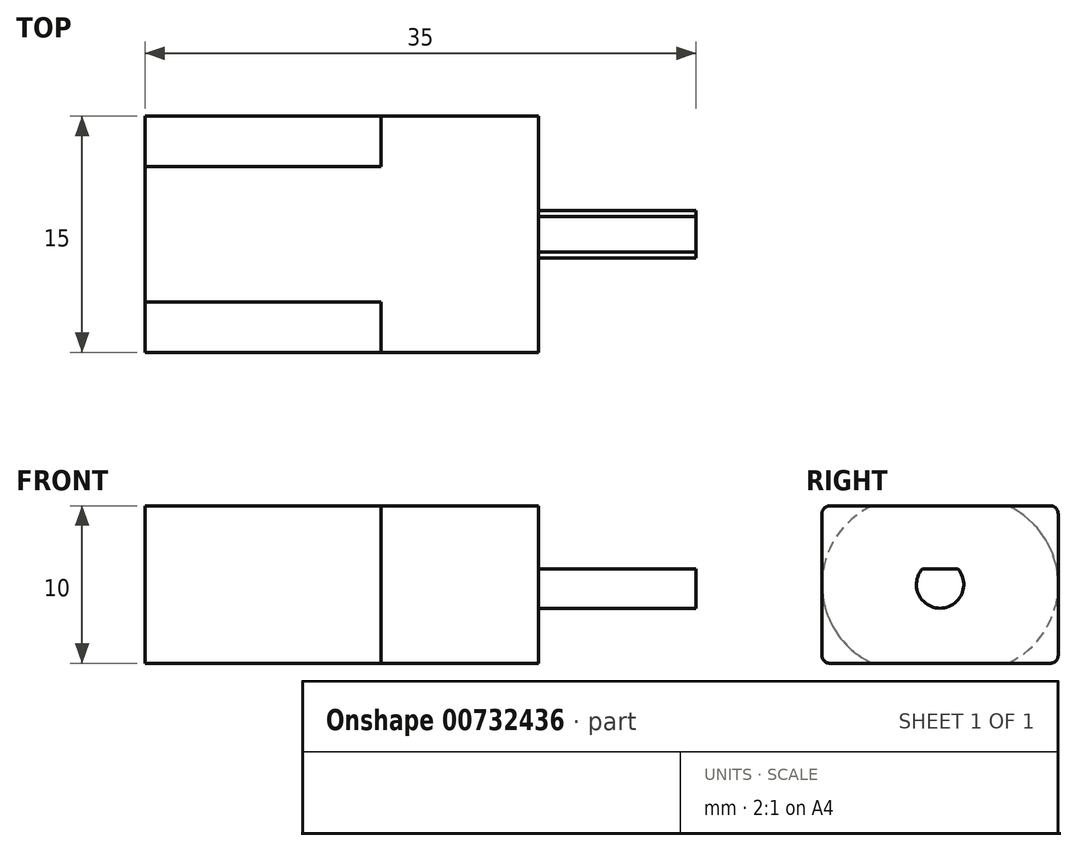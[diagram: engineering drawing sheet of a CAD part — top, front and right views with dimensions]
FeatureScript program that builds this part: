
annotation { "Feature Type Name" : "Feature", "Feature Type Description" : "" }
export const myFeature = defineFeature(function(context is Context, id is Id, definition is map)
    precondition{}
    {
        {
            var Q0;
            Q0=qCreatedBy(makeId("Right.planeOp"),FACE);
            var sketch = newSketch(context, id + "F0", { "sketchPlane" : qUnion([Q0])});
            skLineSegment(sketch, "E0.bottom", {"start": v(-4.3, 5) * mm, "end": v(4.3, 5) * mm});
            skLineSegment(sketch, "E0.top", {"start": v(-4.3, -5) * mm, "end": v(4.3, -5) * mm});
            skLineSegment(sketch, "E1", {"start": v(0, 5) * mm, "end": v(0, 0) * mm, "construction": true});
            skLineSegment(sketch, "E2", {"start": v(0, 0) * mm, "end": v(0, -5) * mm, "construction": true});
            skLineSegment(sketch, "E3", {"start": v(-7.5, 0) * mm, "end": v(0, 0) * mm, "construction": true});
            skLineSegment(sketch, "E4", {"start": v(7.5, 0) * mm, "end": v(0, 0) * mm, "construction": true});
            skArc(sketch, "E5", {"start": v(4.3, -5) * mm, "mid": v(7.5, 0) * mm, "end": v(4.3, 5) * mm});
            skArc(sketch, "E6.MirrorCS", {"start": v(-4.3, -5) * mm, "mid": v(-7.5, 0) * mm, "end": v(-4.3, 5) * mm});
            skSolve(sketch);
        }
        {
            var Q0;
            Q0=makeQuery(id+"F0.imprint","IMPRINT",FACE,{"disambiguationData":[TD([[makeQuery(id+"F0.imprint","IMPRINT",EDGE,{"derivedFrom":sQuery(id+"F0.wireOp",EDGE,"E0.bottom")}),-1.0]])]});
            extrude(context, id + "F1", {"entities" : qUnion([Q0]), "depth" : 15 * mm, "offsetDistance" : 25 * mm});
        }
        {
            var Q0;
            Q0=makeQuery(id+"F1.opExtrude","CAP_FACE",FACE,{"disambiguationData":[OSD([sQuery(id+"F0.wireOp",EDGE,"E0.bottom"),sQuery(id+"F0.wireOp",EDGE,"E0.top"),sQuery(id+"F0.wireOp",EDGE,"E5"),sQuery(id+"F0.wireOp",EDGE,"E6.MirrorCS")])],"isStart":false});
            var sketch = newSketch(context, id + "F2", { "sketchPlane" : qUnion([Q0])});
            skPoint(sketch, "E7.firstSnap0", {"position": v(-7.5, 0) * mm});
            skPoint(sketch, "E7.oppositeSnap0", {"position": v(7.5, 0) * mm});
            skLineSegment(sketch, "E7.bottom", {"start": v(-7.5, 5) * mm, "end": v(7.5, 5) * mm});
            skLineSegment(sketch, "E7.top", {"start": v(-7.5, -5) * mm, "end": v(7.5, -5) * mm});
            skLineSegment(sketch, "E7.left", {"start": v(-7.5, 5) * mm, "end": v(-7.5, -5) * mm});
            skLineSegment(sketch, "E7.right", {"start": v(7.5, 5) * mm, "end": v(7.5, -5) * mm});
            skSolve(sketch);
        }
        {
            var Q0;
            {var subQ0=sQuery(id+"F2.wireOp",EDGE,"E7.bottom");var subQ1=makeQuery(id+"F1.opExtrude","CAP_EDGE",EDGE,{"disambiguationData":[OSD([sQuery(id+"F0.wireOp",EDGE,"E6.MirrorCS")])],"isStart":false});var subQ2=makeQuery(id+"F2.imprint","INTERSECT",VERTEX,{"derivedFrom":[subQ1,subQ0]});Q0=makeQuery(id+"F2.imprint","IMPRINT",FACE,{"disambiguationData":[TD([[makeQuery(id+"F2.imprint","IMPRINT",EDGE,{"disambiguationData":[TD([[subQ2,1.0]])],"derivedFrom":subQ0}),-1.0]])]});}
            var Q1;
            {var subQ0=sQuery(id+"F2.wireOp",EDGE,"E7.bottom");var subQ1=makeQuery(id+"F1.opExtrude","CAP_EDGE",EDGE,{"disambiguationData":[OSD([sQuery(id+"F0.wireOp",EDGE,"E5")])],"isStart":false});var subQ2=makeQuery(id+"F2.imprint","INTERSECT",VERTEX,{"derivedFrom":[subQ1,subQ0]});Q1=makeQuery(id+"F2.imprint","IMPRINT",FACE,{"disambiguationData":[TD([[makeQuery(id+"F2.imprint","IMPRINT",EDGE,{"disambiguationData":[TD([[subQ2,-1.0]])],"derivedFrom":subQ0}),-1.0]])]});}
            var Q2;
            {var subQ0=sQuery(id+"F2.wireOp",EDGE,"E7.bottom");var subQ5=makeQuery(id+"F1.opExtrude","CAP_EDGE",EDGE,{"disambiguationData":[OSD([sQuery(id+"F0.wireOp",EDGE,"E6.MirrorCS")])],"isStart":false});var subQ8=makeQuery(id+"F2.imprint","INTERSECT",VERTEX,{"derivedFrom":[subQ5,subQ0]});Q2=makeQuery(id+"F2.imprint","IMPRINT",FACE,{"disambiguationData":[TD([[makeQuery(id+"F2.imprint","IMPRINT",EDGE,{"disambiguationData":[TD([[subQ8,-1.0]])],"derivedFrom":subQ0}),-1.0]])]});}
            var Q3;
            {var subQ0=sQuery(id+"F2.wireOp",EDGE,"E7.top");var subQ1=makeQuery(id+"F1.opExtrude","CAP_EDGE",EDGE,{"disambiguationData":[OSD([sQuery(id+"F0.wireOp",EDGE,"E6.MirrorCS")])],"isStart":false});var subQ2=makeQuery(id+"F2.imprint","INTERSECT",VERTEX,{"derivedFrom":[subQ1,subQ0]});Q3=makeQuery(id+"F2.imprint","IMPRINT",FACE,{"disambiguationData":[TD([[makeQuery(id+"F2.imprint","IMPRINT",EDGE,{"disambiguationData":[TD([[subQ2,1.0]])],"derivedFrom":subQ0}),1.0]])]});}
            var Q4;
            {var subQ0=sQuery(id+"F2.wireOp",EDGE,"E7.top");var subQ1=makeQuery(id+"F1.opExtrude","CAP_EDGE",EDGE,{"disambiguationData":[OSD([sQuery(id+"F0.wireOp",EDGE,"E5")])],"isStart":false});var subQ2=makeQuery(id+"F2.imprint","INTERSECT",VERTEX,{"derivedFrom":[subQ1,subQ0]});Q4=makeQuery(id+"F2.imprint","IMPRINT",FACE,{"disambiguationData":[TD([[makeQuery(id+"F2.imprint","IMPRINT",EDGE,{"disambiguationData":[TD([[subQ2,-1.0]])],"derivedFrom":subQ0}),1.0]])]});}
            extrude(context, id + "F3", {"entities" : qUnion([Q0, Q1, Q2, Q3, Q4]), "operationType" : NewBodyOperationType.ADD, "depth" : 10 * mm, "offsetDistance" : 25 * mm});
        }
        {
            var Q0;
            Q0=makeQuery(id+"F3.opExtrude","SWEPT_EDGE",EDGE,{"disambiguationData":[OSD([sQuery(id+"F2.wireOp",EDGE,"E7.bottom"),sQuery(id+"F2.wireOp",EDGE,"E7.left")])]});
            var Q1;
            Q1=makeQuery(id+"F3.opExtrude","SWEPT_EDGE",EDGE,{"disambiguationData":[OSD([sQuery(id+"F2.wireOp",EDGE,"E7.bottom"),sQuery(id+"F2.wireOp",EDGE,"E7.right")])]});
            var Q2;
            Q2=makeQuery(id+"F3.opExtrude","SWEPT_EDGE",EDGE,{"disambiguationData":[OSD([sQuery(id+"F2.wireOp",EDGE,"E7.top"),sQuery(id+"F2.wireOp",EDGE,"E7.left")])]});
            var Q3;
            Q3=makeQuery(id+"F3.opExtrude","SWEPT_EDGE",EDGE,{"disambiguationData":[OSD([sQuery(id+"F2.wireOp",EDGE,"E7.top"),sQuery(id+"F2.wireOp",EDGE,"E7.right")])]});
            fillet(context, id + "F4", {"entities" : qUnion([Q0, Q1, Q2, Q3]), "radius" : 0.5 * mm, "tangentPropagation" : true, "defaultsChanged" : false, "vertexSettings" : [], "allowEdgeOverflow" : false});
        }
        {
            var Q0;
            Q0=makeQuery(id+"F3.opExtrude","CAP_FACE",FACE,{"disambiguationData":[OSD([sQuery(id+"F2.wireOp",EDGE,"E7.bottom"),sQuery(id+"F2.wireOp",EDGE,"E7.top"),sQuery(id+"F2.wireOp",EDGE,"E7.left"),sQuery(id+"F2.wireOp",EDGE,"E7.right")])],"isStart":false});
            var sketch = newSketch(context, id + "F5", { "sketchPlane" : qUnion([Q0])});
            skArc(sketch, "E8", {"start": v(-1.12, 1) * mm, "mid": v(0, -1.5) * mm, "end": v(1.12, 1) * mm});
            skLineSegment(sketch, "E9", {"start": v(-1.12, 1) * mm, "end": v(1.12, 1) * mm});
            skSolve(sketch);
        }
        {
            var Q0;
            Q0=makeQuery(id+"F5.imprint","IMPRINT",FACE,{"disambiguationData":[TD([[makeQuery(id+"F5.imprint","IMPRINT",EDGE,{"derivedFrom":sQuery(id+"F5.wireOp",EDGE,"E8")}),1.0]])]});
            extrude(context, id + "F6", {"entities" : qUnion([Q0]), "operationType" : NewBodyOperationType.ADD, "depth" : 10 * mm, "offsetDistance" : 25 * mm});
        }
    });
